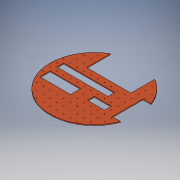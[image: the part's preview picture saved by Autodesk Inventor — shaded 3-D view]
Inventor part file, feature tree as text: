
AUTODESK INVENTOR PART (.ipt)
format: ipt  version: 2018 (Build 220112000, 112)  size: 250,880 bytes
history: native  units: in
note: dims shown in document units (in); Inventor stores cm internally (conversion verified against a paired STEP export)
features: sketch x3, extrude x2, hole x1, pattern_linear x1
ambient origin geometry x8: Origin, YZ Plane, XZ Plane, XY Plane, X Axis, Y Axis, Z Axis, Center Point
bodies: Solid1 (feature_tree)
feature tree (7):
  extrude  "Extrusion1"  Depth=0.125in TaperAngle=0.0deg
  extrude  "Extrusion2"  TaperAngle=90.0deg  [1 undecoded]
  hole  "Hole1"  [1 undecoded]
  pattern_linear  "Rectangular Pattern1"  Spacing1=90.0deg  [1 undecoded]
  sketch  "Sketch1"  dims[d0=13.0in d1=0.125in d2=0.0in]
  sketch  "Sketch2"  dims[d3=3.5in d4=90.0deg]
  sketch  "Sketch3"  dims[d5=6.5in d6=3.5in d7=90.0deg d8=5.0in d10=7.5in d11=1.0in d12=1.0in d13=4.5in d14=1.5in d15=1.0in d16=1.125in d17=2.5in d18=1.0in d19=1.0in d20=2.0in d21=1.2in d22=1.2in d23=4.5in d24=3.0in d25=0.125in d26=0.0in d27=0.5in d28=0.085in d29=0.224in d30=0.375in d31=0.25in d32=0.5635in d33=0.349in d34=0.8108in d35=5.1181in d37=1.0in d38=5.1181in d40=1.0in d41=270.0deg]
note: 3 required parameter values undecoded (feature->parameter linkage not recoverable at this tier; creation-order binding heuristic only, values carry confidence <= 0.55)
